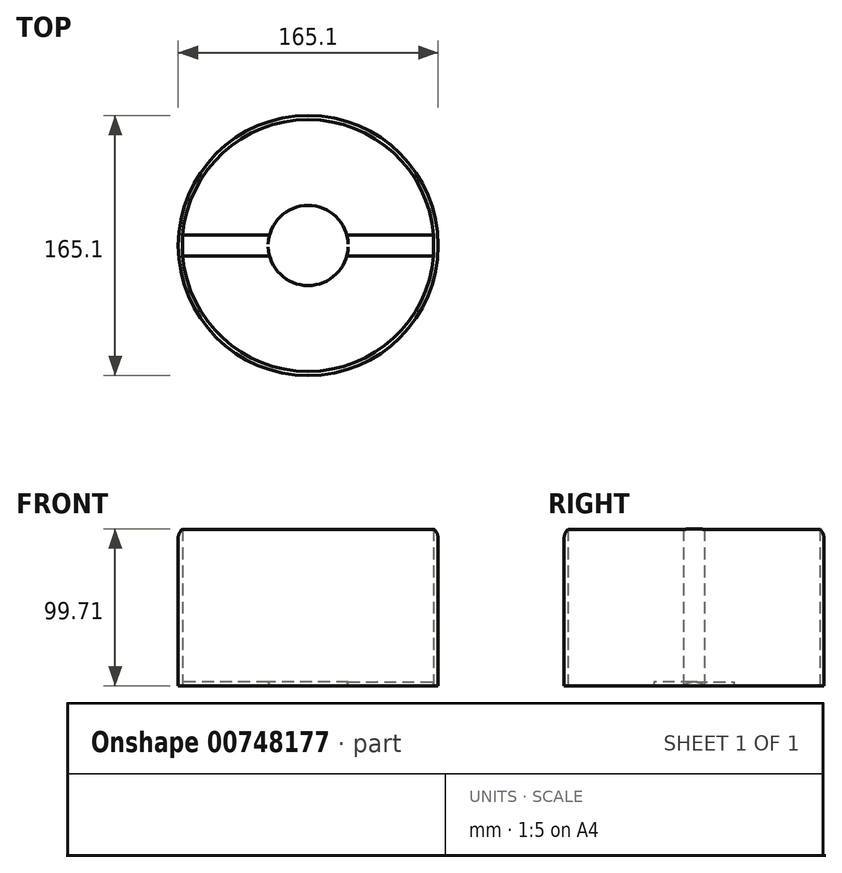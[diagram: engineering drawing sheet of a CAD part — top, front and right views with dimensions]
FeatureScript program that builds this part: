
annotation { "Feature Type Name" : "Feature", "Feature Type Description" : "" }
export const myFeature = defineFeature(function(context is Context, id is Id, definition is map)
    precondition{}
    {
        {
            var Q0;
            Q0=qCreatedBy(makeId("Top.planeOp"),FACE);
            var sketch = newSketch(context, id + "F0", { "sketchPlane" : qUnion([Q0])});
            skCircle(sketch, "E0", {"center": v(0, 0) * mm, "radius": 82.55 * mm});
            skArc(sketch, "E1", {"start": v(79.73, 6.7) * mm, "mid": v(0, 80.01) * mm, "end": v(-79.73, 6.7) * mm});
            skArc(sketch, "E2", {"start": v(-10.85, 22.96) * mm, "mid": v(-19.46, 16.32) * mm, "end": v(-24.5, 6.7) * mm});
            skLineSegment(sketch, "E3", {"start": v(-79.73, 6.7) * mm, "end": v(-24.5, 6.7) * mm});
            skLineSegment(sketch, "E4", {"start": v(79.73, -6.7) * mm, "end": v(24.5, -6.7) * mm});
            skLineSegment(sketch, "E5.trimOffspring", {"start": v(24.5, 6.7) * mm, "end": v(79.73, 6.7) * mm});
            skLineSegment(sketch, "E6.trimOffspring", {"start": v(-24.5, -6.7) * mm, "end": v(-79.73, -6.7) * mm});
            skArc(sketch, "E7.trimOffspring", {"start": v(-79.73, -6.7) * mm, "mid": v(0, -80) * mm, "end": v(79.73, -6.7) * mm});
            skArc(sketch, "E8.trimOffspring", {"start": v(-24.5, -6.7) * mm, "mid": v(0, -25.4) * mm, "end": v(24.5, -6.7) * mm});
            skArc(sketch, "E9.trimOffspring", {"start": v(24.5, 6.7) * mm, "mid": v(19.46, 16.32) * mm, "end": v(10.85, 22.96) * mm});
            skLineSegment(sketch, "E10", {"start": v(-79.73, 6.7) * mm, "end": v(-79.73, -6.7) * mm});
            skLineSegment(sketch, "E11", {"start": v(79.73, 6.7) * mm, "end": v(79.73, -6.7) * mm});
            skArc(sketch, "E12", {"start": v(10.85, 22.96) * mm, "mid": v(0, 25.4) * mm, "end": v(-10.85, 22.96) * mm});
            skSolve(sketch);
        }
        {
            var Q0;
            Q0 = qSketchRegion(id + "F0", true);
            extrude(context, id + "F1", {"entities" : qUnion([Q0]), "depth" : 101.6 * mm, "offsetDistance" : 25.4 * mm});
        }
        {
            var Q0;
            Q0=makeQuery(id+"F0.imprint","IMPRINT",FACE,{"disambiguationData":[TD([[makeQuery(id+"F0.imprint","IMPRINT",EDGE,{"derivedFrom":sQuery(id+"F0.wireOp",EDGE,"E2")}),1.0]])]});
            extrude(context, id + "F2", {"entities" : qUnion([Q0]), "operationType" : NewBodyOperationType.ADD, "depth" : 2.54 * mm, "offsetDistance" : 25.4 * mm});
        }
        {
            var Q0;
            Q0=makeQuery(id+"F2.opExtrude","CAP_EDGE",EDGE,{"disambiguationData":[OSD([sQuery(id+"F0.wireOp",EDGE,"E3")])],"isStart":false});
            var Q1;
            Q1=makeQuery(id+"F2.opExtrude","CAP_EDGE",EDGE,{"disambiguationData":[OSD([sQuery(id+"F0.wireOp",EDGE,"E6.trimOffspring")])],"isStart":false});
            var Q2;
            Q2=makeQuery(id+"F2.opExtrude","CAP_EDGE",EDGE,{"disambiguationData":[OSD([sQuery(id+"F0.wireOp",EDGE,"E5.trimOffspring")])],"isStart":false});
            var Q3;
            Q3=makeQuery(id+"F2.opExtrude","CAP_EDGE",EDGE,{"disambiguationData":[OSD([sQuery(id+"F0.wireOp",EDGE,"E4")])],"isStart":false});
            var Q4;
            Q4=makeQuery(id+"F1.opExtrude","CAP_EDGE",EDGE,{"disambiguationData":[OSD([sQuery(id+"F0.wireOp",EDGE,"E0")])],"isStart":false});
            fillet(context, id + "F3", {"entities" : qUnion([Q0, Q1, Q2, Q3, Q4]), "radius" : 7.97 * mm, "tangentPropagation" : true, "allowEdgeOverflow" : false});
        }
    });
